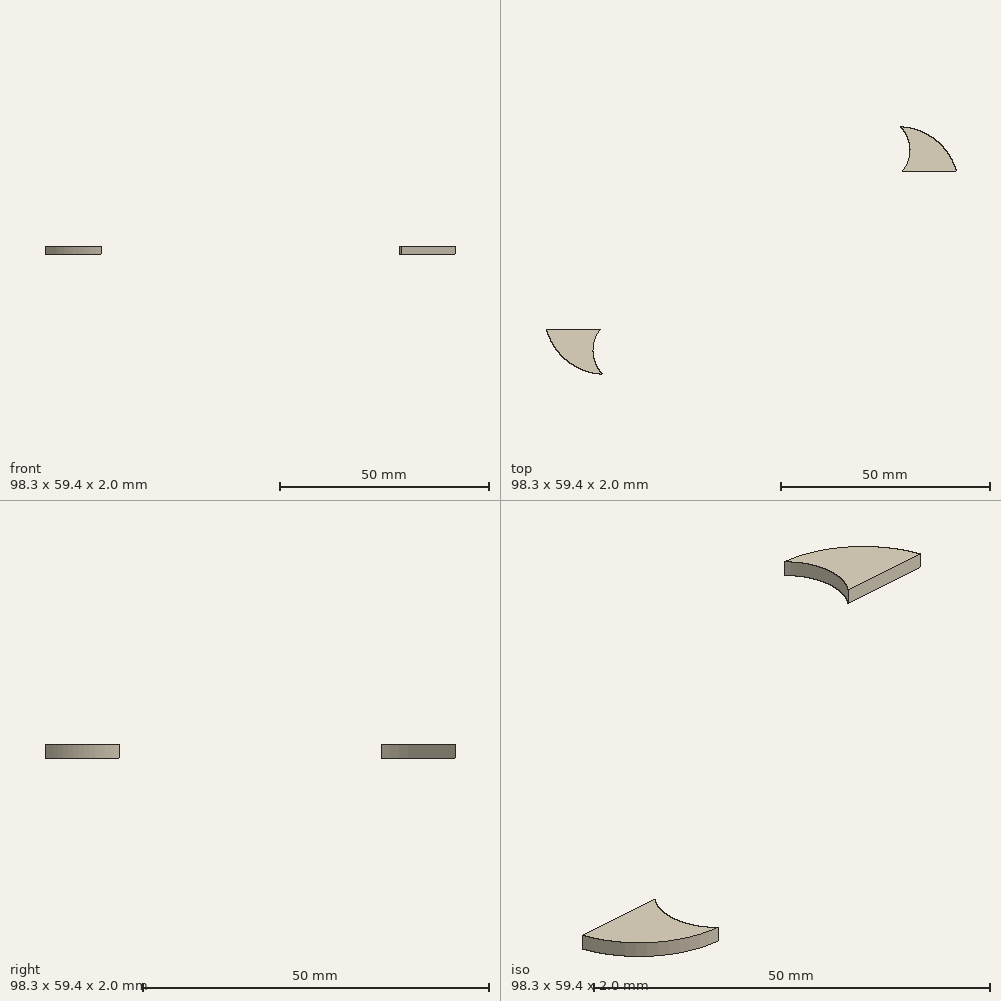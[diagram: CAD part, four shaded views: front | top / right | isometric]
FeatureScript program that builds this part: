
annotation { "Feature Type Name" : "Feature", "Feature Type Description" : "" }
export const myFeature = defineFeature(function(context is Context, id is Id, definition is map)
    precondition{}
    {
        {
            var Q0;
            Q0=qCreatedBy(makeId("Top.planeOp"),FACE);
            var sketch = newSketch(context, id + "F0", { "sketchPlane" : qUnion([Q0])});
            skLineSegment(sketch, "E0.bottom", {"start": v(0, 0) * mm, "end": v(106, 0) * mm});
            skLineSegment(sketch, "E0.top", {"start": v(0, 66) * mm, "end": v(106, 66) * mm});
            skLineSegment(sketch, "E0.left", {"start": v(0, 0) * mm, "end": v(0, 66) * mm});
            skLineSegment(sketch, "E0.right", {"start": v(106, 0) * mm, "end": v(106, 66) * mm});
            skPoint(sketch, "E1", {"position": v(0, 48) * mm});
            skPoint(sketch, "E2", {"position": v(0, 14) * mm});
            skPoint(sketch, "E3", {"position": v(18, 66) * mm});
            skPoint(sketch, "E4", {"position": v(86, 66) * mm});
            skArc(sketch, "E5", {"start": v(18, 66) * mm, "mid": v(5.27, 60.73) * mm, "end": v(0, 48) * mm});
            skLineSegment(sketch, "E6", {"start": v(53, 66) * mm, "end": v(53, 0) * mm, "construction": true});
            skLineSegment(sketch, "E7", {"start": v(0, 33) * mm, "end": v(106, 33) * mm, "construction": true});
            skArc(sketch, "E8.MirrorCS", {"start": v(88, 66) * mm, "mid": v(100.73, 60.73) * mm, "end": v(106, 48) * mm});
            skArc(sketch, "E9.MirrorCS", {"start": v(18, 0) * mm, "mid": v(5.27, 5.27) * mm, "end": v(0, 18) * mm});
            skArc(sketch, "E10.MirrorCS", {"start": v(88, 0) * mm, "mid": v(100.73, 5.27) * mm, "end": v(106, 18) * mm});
            skSolve(sketch);
        }
        {
            var Q0;
            {var subQ3=sQuery(id+"F0.wireOp",EDGE,"E5");Q0=makeQuery(id+"F0.imprint","IMPRINT",FACE,{"disambiguationData":[TD([[makeQuery(id+"F0.imprint","IMPRINT",EDGE,{"derivedFrom":subQ3}),1.0]])]});}
            extrude(context, id + "F1", {"entities" : qUnion([Q0]), "depth" : 2 * mm, "offsetDistance" : 25 * mm});
        }
        {
            var Q0;
            Q0=makeQuery(id+"F1.opExtrude","CAP_FACE",FACE,{"disambiguationData":[OSD([sQuery(id+"F0.wireOp",EDGE,"E0.bottom"),sQuery(id+"F0.wireOp",EDGE,"E0.top"),sQuery(id+"F0.wireOp",EDGE,"E0.left"),sQuery(id+"F0.wireOp",EDGE,"E0.right"),sQuery(id+"F0.wireOp",EDGE,"E5"),sQuery(id+"F0.wireOp",EDGE,"E8.MirrorCS"),sQuery(id+"F0.wireOp",EDGE,"E9.MirrorCS"),sQuery(id+"F0.wireOp",EDGE,"E10.MirrorCS")])],"isStart":false});
            var sketch = newSketch(context, id + "F2", { "sketchPlane" : qUnion([Q0])});
            skText(sketch, "E11", { "text": "AMY", "fontName": "AllertaStencil-Regular.ttf"});
            skLineSegment(sketch, "E12.bottom", {"start": v(23, 62) * mm, "end": v(83, 62) * mm});
            skLineSegment(sketch, "E12.top", {"start": v(23, 52) * mm, "end": v(83, 52) * mm});
            skLineSegment(sketch, "E12.left", {"start": v(18, 57) * mm, "end": v(18, 57) * mm});
            skLineSegment(sketch, "E12.right", {"start": v(88, 57) * mm, "end": v(88, 57) * mm});
            skPoint(sketch, "E13.visualSharp", {"position": v(18, 62) * mm});
            skArc(sketch, "E13.filletArc", {"start": v(23, 62) * mm, "mid": v(19.46, 60.54) * mm, "end": v(18, 57) * mm});
            skPoint(sketch, "E14.visualSharp", {"position": v(18, 52) * mm});
            skArc(sketch, "E14.filletArc", {"start": v(18, 57) * mm, "mid": v(19.46, 53.46) * mm, "end": v(23, 52) * mm});
            skPoint(sketch, "E15.visualSharp", {"position": v(88, 62) * mm});
            skArc(sketch, "E15.filletArc", {"start": v(88, 57) * mm, "mid": v(86.54, 60.54) * mm, "end": v(83, 62) * mm});
            skPoint(sketch, "E16.visualSharp", {"position": v(88, 52) * mm});
            skArc(sketch, "E16.filletArc", {"start": v(83, 52) * mm, "mid": v(86.54, 53.46) * mm, "end": v(88, 57) * mm});
            skArc(sketch, "E17.0", {"start": v(15, 57) * mm, "mid": v(15.45, 54.35) * mm, "end": v(16.76, 52) * mm});
            skArc(sketch, "E17.1", {"start": v(17.37, 62.69) * mm, "mid": v(15.62, 60.08) * mm, "end": v(15, 57) * mm});
            skArc(sketch, "E18.0", {"start": v(17.37, 62.69) * mm, "mid": v(8.88, 59.53) * mm, "end": v(3.85, 52) * mm});
            skLineSegment(sketch, "E19", {"start": v(16.76, 52) * mm, "end": v(3.85, 52) * mm});
            skLineSegment(sketch, "E20", {"start": v(0, 33) * mm, "end": v(106, 33) * mm, "construction": true});
            skLineSegment(sketch, "E21.MirrorCS", {"start": v(23, 14) * mm, "end": v(83, 14) * mm});
            skArc(sketch, "E22.MirrorCS", {"start": v(18, 9) * mm, "mid": v(19.46, 12.54) * mm, "end": v(23, 14) * mm});
            skArc(sketch, "E23.MirrorCS", {"start": v(23, 4) * mm, "mid": v(19.46, 5.46) * mm, "end": v(18, 9) * mm});
            skLineSegment(sketch, "E24.MirrorCS", {"start": v(23, 4) * mm, "end": v(83, 4) * mm});
            skArc(sketch, "E25.MirrorCS", {"start": v(88, 9) * mm, "mid": v(86.54, 5.46) * mm, "end": v(83, 4) * mm});
            skArc(sketch, "E26.MirrorCS", {"start": v(83, 14) * mm, "mid": v(86.54, 12.54) * mm, "end": v(88, 9) * mm});
            skArc(sketch, "E27.MirrorCS", {"start": v(17.37, 3.31) * mm, "mid": v(15.62, 5.92) * mm, "end": v(15, 9) * mm});
            skArc(sketch, "E28.MirrorCS", {"start": v(17.37, 3.31) * mm, "mid": v(8.88, 6.47) * mm, "end": v(3.85, 14) * mm});
            skLineSegment(sketch, "E29.MirrorCS", {"start": v(16.76, 14) * mm, "end": v(3.85, 14) * mm});
            skArc(sketch, "E30.MirrorCS", {"start": v(15, 9) * mm, "mid": v(15.45, 11.65) * mm, "end": v(16.76, 14) * mm});
            skCircle(sketch, "E31", {"center": v(98, 21.8) * mm, "radius": 4 * mm});
            skLineSegment(sketch, "E32", {"start": v(53, 66) * mm, "end": v(53, 0) * mm, "construction": true});
            skArc(sketch, "E33.MirrorCS", {"start": v(88.63, 62.69) * mm, "mid": v(90.38, 60.08) * mm, "end": v(91, 57) * mm});
            skArc(sketch, "E34.MirrorCS", {"start": v(88.63, 62.69) * mm, "mid": v(97.12, 59.53) * mm, "end": v(102.15, 52) * mm});
            skLineSegment(sketch, "E35.MirrorCS", {"start": v(89.24, 52) * mm, "end": v(102.15, 52) * mm});
            skArc(sketch, "E36.MirrorCS", {"start": v(91, 57) * mm, "mid": v(90.55, 54.35) * mm, "end": v(89.24, 52) * mm});
            skArc(sketch, "E37.MirrorCS", {"start": v(91, 9) * mm, "mid": v(90.55, 11.65) * mm, "end": v(89.24, 14) * mm});
            skLineSegment(sketch, "E38.MirrorCS", {"start": v(89.24, 14) * mm, "end": v(102.15, 14) * mm});
            skArc(sketch, "E39.MirrorCS", {"start": v(88.63, 3.31) * mm, "mid": v(97.12, 6.47) * mm, "end": v(102.15, 14) * mm});
            skArc(sketch, "E40.MirrorCS", {"start": v(88.63, 3.31) * mm, "mid": v(90.38, 5.92) * mm, "end": v(91, 9) * mm});
            const initialGuessF2  = {"E11": [0, 0.0178, 1, 0, 0.0302]};
            skSetInitialGuess(sketch, initialGuessF2);
            skSolve(sketch);
        }
        {
            var Q0;
            Q0=makeQuery(id+"F2.imprint","IMPRINT",FACE,{"disambiguationData":[TD([[makeQuery(id+"F2.imprint","IMPRINT",EDGE,{"derivedFrom":sQuery(id+"F2.wireOp",EDGE,"E11.sketch_text.stroke-0")}),-1.0]])]});
            var Q1;
            Q1=makeQuery(id+"F2.imprint","IMPRINT",FACE,{"disambiguationData":[TD([[makeQuery(id+"F2.imprint","IMPRINT",EDGE,{"derivedFrom":sQuery(id+"F2.wireOp",EDGE,"E11.sketch_text.stroke-7")}),-1.0]])]});
            var Q2;
            Q2=makeQuery(id+"F2.imprint","IMPRINT",FACE,{"disambiguationData":[TD([[makeQuery(id+"F2.imprint","IMPRINT",EDGE,{"derivedFrom":sQuery(id+"F2.wireOp",EDGE,"E11.sketch_text.stroke-11")}),-1.0]])]});
            var Q3;
            Q3=makeQuery(id+"F2.imprint","IMPRINT",FACE,{"disambiguationData":[TD([[makeQuery(id+"F2.imprint","IMPRINT",EDGE,{"derivedFrom":sQuery(id+"F2.wireOp",EDGE,"E11.sketch_text.stroke-19")}),-1.0]])]});
            var Q4;
            Q4=makeQuery(id+"F2.imprint","IMPRINT",FACE,{"disambiguationData":[TD([[makeQuery(id+"F2.imprint","IMPRINT",EDGE,{"derivedFrom":sQuery(id+"F2.wireOp",EDGE,"E11.sketch_text.stroke-27")}),-1.0]])]});
            var Q5;
            Q5=makeQuery(id+"F2.imprint","IMPRINT",FACE,{"disambiguationData":[TD([[makeQuery(id+"F2.imprint","IMPRINT",EDGE,{"derivedFrom":sQuery(id+"F2.wireOp",EDGE,"E11.sketch_text.stroke-33")}),-1.0]])]});
            var Q6;
            Q6=makeQuery(id+"F2.imprint","IMPRINT",FACE,{"disambiguationData":[TD([[makeQuery(id+"F2.imprint","IMPRINT",EDGE,{"derivedFrom":sQuery(id+"F2.wireOp",EDGE,"E17.0")}),-1.0]])]});
            var Q7;
            Q7=makeQuery(id+"F2.imprint","IMPRINT",FACE,{"disambiguationData":[TD([[makeQuery(id+"F2.imprint","IMPRINT",EDGE,{"derivedFrom":sQuery(id+"F2.wireOp",EDGE,"E27.MirrorCS")}),1.0]])]});
            var Q8;
            Q8=makeQuery(id+"F2.imprint","IMPRINT",FACE,{"disambiguationData":[TD([[makeQuery(id+"F2.imprint","IMPRINT",EDGE,{"derivedFrom":sQuery(id+"F2.wireOp",EDGE,"E31")}),1.0]])]});
            var Q9;
            {var subQ8=sQuery(id+"F2.wireOp",EDGE,"E12.bottom");Q9=makeQuery(id+"F2.imprint","IMPRINT",FACE,{"disambiguationData":[TD([[makeQuery(id+"F2.imprint","IMPRINT",EDGE,{"derivedFrom":subQ8}),-1.0]])]});}
            var Q10;
            {var subQ0=sQuery(id+"F2.wireOp",EDGE,"555ab043-93ba-4d2c-84f4-d5ec9d1850120.MirrorCS");Q10=makeQuery(id+"F2.imprint","IMPRINT",FACE,{"disambiguationData":[TD([[makeQuery(id+"F2.imprint","IMPRINT",EDGE,{"derivedFrom":subQ0}),1.0]])]});}
            var Q11;
            {var subQ1=sQuery(id+"F2.wireOp",EDGE,"E21.MirrorCS");Q11=makeQuery(id+"F2.imprint","IMPRINT",FACE,{"disambiguationData":[TD([[makeQuery(id+"F2.imprint","IMPRINT",EDGE,{"derivedFrom":subQ1}),-1.0]])]});}
            var Q12;
            {var subQ0=sQuery(id+"F2.wireOp",EDGE,"E26.MirrorCS");var subQ1=sQuery(id+"F2.wireOp",EDGE,"E25.MirrorCS");var subQ2=makeQuery(id+"F2.imprint","INTERSECT",VERTEX,{"derivedFrom":[subQ1,subQ0]});Q12=makeQuery(id+"F2.imprint","IMPRINT",FACE,{"disambiguationData":[TD([[makeQuery(id+"F2.imprint","IMPRINT",EDGE,{"disambiguationData":[TD([[subQ2,-1.0]])],"derivedFrom":subQ1}),-1.0]])]});}
            var Q13;
            {var subQ0=sQuery(id+"F2.wireOp",EDGE,"bf1d3228-243b-4859-836a-fcda7ff654080.MirrorCS");Q13=makeQuery(id+"F2.imprint","IMPRINT",FACE,{"disambiguationData":[TD([[makeQuery(id+"F2.imprint","IMPRINT",EDGE,{"derivedFrom":subQ0}),1.0]])]});}
            var Q14;
            {var subQ0=sQuery(id+"F2.wireOp",EDGE,"E16.filletArc");var subQ1=sQuery(id+"F2.wireOp",EDGE,"E15.filletArc");var subQ2=makeQuery(id+"F2.imprint","INTERSECT",VERTEX,{"derivedFrom":[subQ1,subQ0]});Q14=makeQuery(id+"F2.imprint","IMPRINT",FACE,{"disambiguationData":[TD([[makeQuery(id+"F2.imprint","IMPRINT",EDGE,{"disambiguationData":[TD([[subQ2,-1.0]])],"derivedFrom":subQ1}),1.0]])]});}
            var Q15;
            Q15=makeQuery(id+"F2.imprint","IMPRINT",FACE,{"disambiguationData":[TD([[makeQuery(id+"F2.imprint","IMPRINT",EDGE,{"derivedFrom":sQuery(id+"F2.wireOp",EDGE,"E33.MirrorCS")}),1.0]])]});
            var Q16;
            Q16=makeQuery(id+"F2.imprint","IMPRINT",FACE,{"disambiguationData":[TD([[makeQuery(id+"F2.imprint","IMPRINT",EDGE,{"derivedFrom":sQuery(id+"F2.wireOp",EDGE,"E38.MirrorCS")}),-1.0]])]});
            extrude(context, id + "F3", {"entities" : qUnion([Q0, Q1, Q2, Q3, Q4, Q5, Q6, Q7, Q8, Q9, Q10, Q11, Q12, Q13, Q14, Q15, Q16]), "operationType" : NewBodyOperationType.REMOVE, "endBound" : BoundingType.UP_TO_NEXT, "oppositeDirection" : true, "depth" : 25 * mm, "offsetDistance" : 25 * mm});
        }
    });
